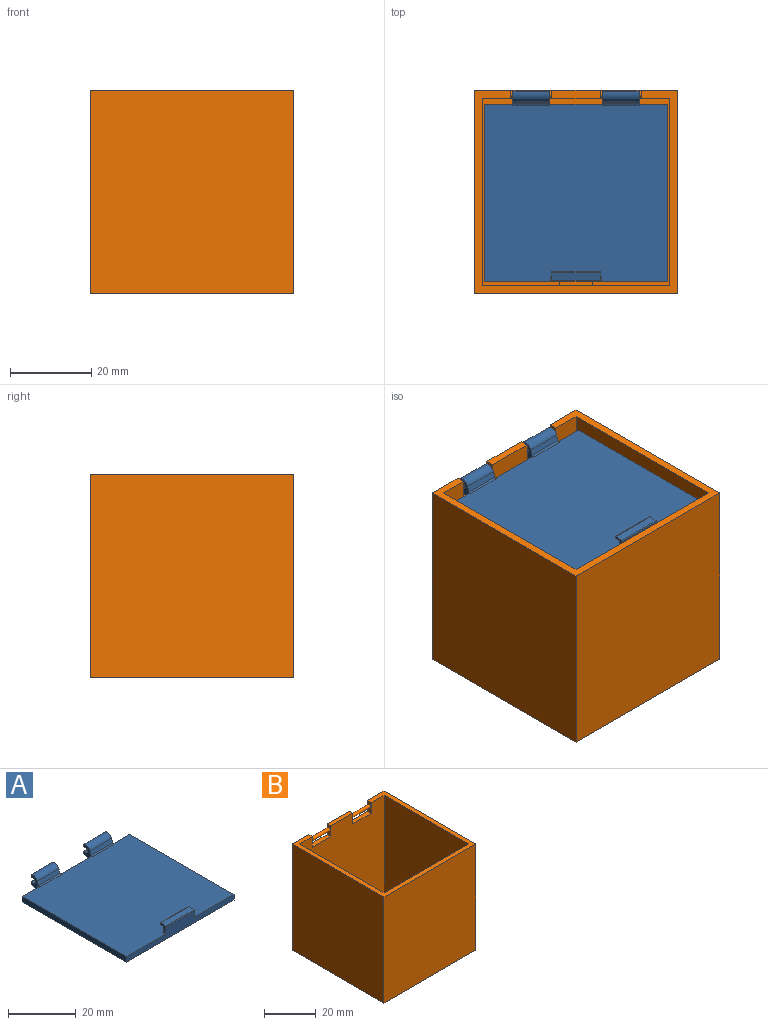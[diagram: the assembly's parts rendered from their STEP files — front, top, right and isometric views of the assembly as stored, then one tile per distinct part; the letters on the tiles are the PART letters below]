
ASSEMBLY  parts=2 mates=1
PART A: 43 faces, bbox 45x46.7x5 mm
  f0: plane 7x2mm, normal (0,1,0), area 14mm2, adj f3,f5,f7,f18
  f1: plane 13x2mm, normal (0,1,0), area 26mm2, adj f3,f5,f13,f19
  f2: plane 7x2mm, normal (0,1,0), area 14mm2, adj f3,f5,f6,f12
  f3: plane 45x43.6mm, normal (0,0,1), area 1940.7mm2, adj f0,f1,f2,f4,f6,f7,f12,f13
  f4: plane 45x4.43mm, normal (0,-1,0), area 119.1mm2, adj f3,f5,f6,f7,f32,f33,f34,f35
  f5: plane 45x43.6mm, normal (0,0,-1), area 1962mm2, adj f0,f1,f2,f4,f6,f7,f9,f16
  f6: plane 43.6x2mm, normal (1,0,0), area 87.2mm2, adj f2,f3,f4,f5
  f7: plane 43.6x2mm, normal (-1,0,0), area 87.2mm2, adj f0,f3,f4,f5
  f8: plane 9x1.39mm, normal (0,-0.94,0.33), area 13.3mm2, adj f10,f12,f13,f42
  f9: plane 9x3.1mm, normal (0,0.39,-0.92), area 30.4mm2, adj f5,f12,f13,f22
  f10: cylinder r=1.9mm len=9mm, axis (-1,0,0), area 27.5mm2, adj f8,f12,f13,f23
  f11: cylinder r=0.9mm len=9mm, axis (-1,0,0), area 35.9mm2, adj f12,f13,f24,f25
  f12: plane 5x3.45mm, normal (1,0,0), area 9.1mm2, adj f2,f3,f8,f9,f10,f11,f22,f23
  f13: plane 5x3.45mm, normal (-1,0,0), area 9.1mm2, adj f1,f3,f8,f9,f10,f11,f22,f23
  f14: plane 9x1.39mm, normal (0,-0.94,0.33), area 13.3mm2, adj f15,f18,f19,f41
  f15: cylinder r=1.9mm len=9mm, axis (1,0,0), area 27.5mm2, adj f14,f18,f19,f20
  f16: plane 9x3.1mm, normal (0,0.39,-0.92), area 30.4mm2, adj f5,f18,f19,f21
  f17: cylinder r=0.9mm len=9mm, axis (1,0,0), area 35.9mm2, adj f18,f19,f26,f27
  f18: plane 5x3.45mm, normal (-1,0,0), area 9.1mm2, adj f0,f3,f14,f15,f16,f17,f20,f21
  f19: plane 5x3.45mm, normal (1,0,0), area 9.1mm2, adj f1,f3,f14,f15,f16,f17,f20,f21
  f20: plane 9x0.97mm, normal (0,1,0), area 8.7mm2, adj f15,f18,f19,f27
  f21: plane 9x0.97mm, normal (0,1,0), area 8.7mm2, adj f16,f18,f19,f26
  f22: plane 9x0.97mm, normal (0,1,0), area 8.7mm2, adj f9,f12,f13,f25
  f23: plane 9x0.97mm, normal (0,1,0), area 8.7mm2, adj f10,f12,f13,f24
  f24: cylinder r=0.1mm len=9mm, axis (-1,0,0), area 2mm2, adj f11,f12,f13,f23
  f25: cylinder r=0.1mm len=9mm, axis (-1,0,0), area 2mm2, adj f11,f12,f13,f22
  f26: cylinder r=0.1mm len=9mm, axis (1,0,0), area 2mm2, adj f17,f18,f19,f21
  f27: cylinder r=0.1mm len=9mm, axis (1,0,0), area 2mm2, adj f17,f18,f19,f20
  f28: plane 12x1.8mm, normal (0,1,0), area 21.6mm2, adj f32,f33,f36,f37
  f29: plane 12x0.97mm, normal (0,0.17,-0.98), area 11.8mm2, adj f32,f33,f37,f38
  f30: plane 12x0.19mm, normal (0,1,0), area 2.3mm2, adj f32,f33,f38,f39
  f31: plane 12x1.9mm, normal (0,-0.17,0.98), area 23.2mm2, adj f32,f33,f39,f40
  f32: plane 2.76x2.3mm, normal (1,0,0), area 3.2mm2, adj f4,f28,f29,f30,f31,f34,f37,f38
  f33: plane 2.76x2.3mm, normal (-1,0,0), area 3.2mm2, adj f4,f28,f29,f30,f31,f35,f37,f38
  f34: cylinder r=0.2mm len=1.2mm, axis (0,1,0), area 0.3mm2, adj f3,f4,f32,f36
  f35: cylinder r=0.2mm len=1.2mm, axis (0,-1,0), area 0.3mm2, adj f3,f4,f33,f36
  f36: cylinder r=0.2mm len=12.4mm, axis (1,0,0), area 3.8mm2, adj f3,f28,f34,f35
  f37: cylinder r=0.2mm len=12mm, axis (1,0,0), area 3.4mm2, adj f28,f29,f32,f33
  f38: cylinder r=0.2mm len=12mm, axis (-1,0,0), area 3.4mm2, adj f29,f30,f32,f33
  f39: cylinder r=0.2mm len=12mm, axis (1,0,0), area 4.2mm2, adj f30,f31,f32,f33
  f40: cylinder r=0.2mm len=12mm, axis (1,0,0), area 3.4mm2, adj f4,f31,f32,f33
  f41: cylinder r=0.5mm len=9mm, axis (-1,0,0), area 5.5mm2, adj f3,f14,f18,f19
  f42: cylinder r=0.5mm len=9mm, axis (-1,0,0), area 5.5mm2, adj f3,f8,f12,f13
PART B: 25 faces, bbox 50x50x50 mm
  f0: plane 12x2mm, normal (0,0,1), area 24mm2, adj f2,f3,f13,f17
  f1: plane 50x50mm, normal (0,0,1), area 320mm2, adj f2,f3,f4,f5,f6,f8,f9,f10
  f2: plane 50x50mm, normal (0,1,0), area 2400mm2, adj f0,f1,f4,f5,f7,f12,f13,f14
  f3: plane 48x46mm, normal (0,-1,0), area 2108mm2, adj f0,f1,f8,f9,f11,f12,f13,f14
  f4: plane 50x50mm, normal (1,0,0), area 2500mm2, adj f1,f2,f6,f7
  f5: plane 50x50mm, normal (-1,0,0), area 2500mm2, adj f1,f2,f6,f7
  f6: plane 50x50mm, normal (0,-1,0), area 2500mm2, adj f1,f4,f5,f7
  f7: plane 50x50mm, normal (0,0,-1), area 2500mm2, adj f2,f4,f5,f6
  f8: plane 48x46mm, normal (-1,0,0), area 2208mm2, adj f1,f3,f10,f11
  f9: plane 48x46mm, normal (1,0,0), area 2208mm2, adj f1,f3,f10,f11
  f10: plane 48x46mm, normal (0,1,0), area 2176mm2, adj f1,f8,f9,f11,f20,f21,f22,f23
  f11: plane 46x46mm, normal (0,0,1), area 2116mm2, adj f3,f8,f9,f10
  f12: plane 5x2mm, normal (1,0,0), area 8.2mm2, adj f1,f2,f3,f14,f19
  f13: plane 5x2mm, normal (-1,0,0), area 8.2mm2, adj f0,f2,f3,f14,f19
  f14: plane 10x2mm, normal (0,0,1), area 20mm2, adj f2,f3,f12,f13
  f15: plane 5x2mm, normal (-1,0,0), area 8.2mm2, adj f1,f2,f3,f16,f18
  f16: plane 10x2mm, normal (0,0,1), area 20mm2, adj f2,f3,f15,f17
  f17: plane 5x2mm, normal (1,0,0), area 8.2mm2, adj f0,f2,f3,f16,f18
  f18: cylinder r=0.75mm len=10mm, axis (-1,0,0), area 47.1mm2, adj f15,f17
  f19: cylinder r=0.75mm len=10mm, axis (-1,0,0), area 47.1mm2, adj f12,f13
  f20: plane 8x2.72mm, normal (0,0.8,-0.6), area 27.2mm2, adj f10,f22,f23,f24
  f21: plane 8x1.4mm, normal (0,0,1), area 11.2mm2, adj f10,f22,f23,f24
  f22: plane 4x2.2mm, normal (1,0,0), area 5.4mm2, adj f10,f20,f21,f24
  f23: plane 4x2.2mm, normal (-1,0,0), area 5.4mm2, adj f10,f20,f21,f24
  f24: cylinder r=0.8mm len=8mm, axis (-1,0,0), area 14.2mm2, adj f20,f21,f22,f23
PLACE A t=(0,21.6,46.9)mm
PLACE B at identity fixed
MATE revolute B.f18 <-> A.f10  axis (-1,0,0) through (16,24,48)mm
